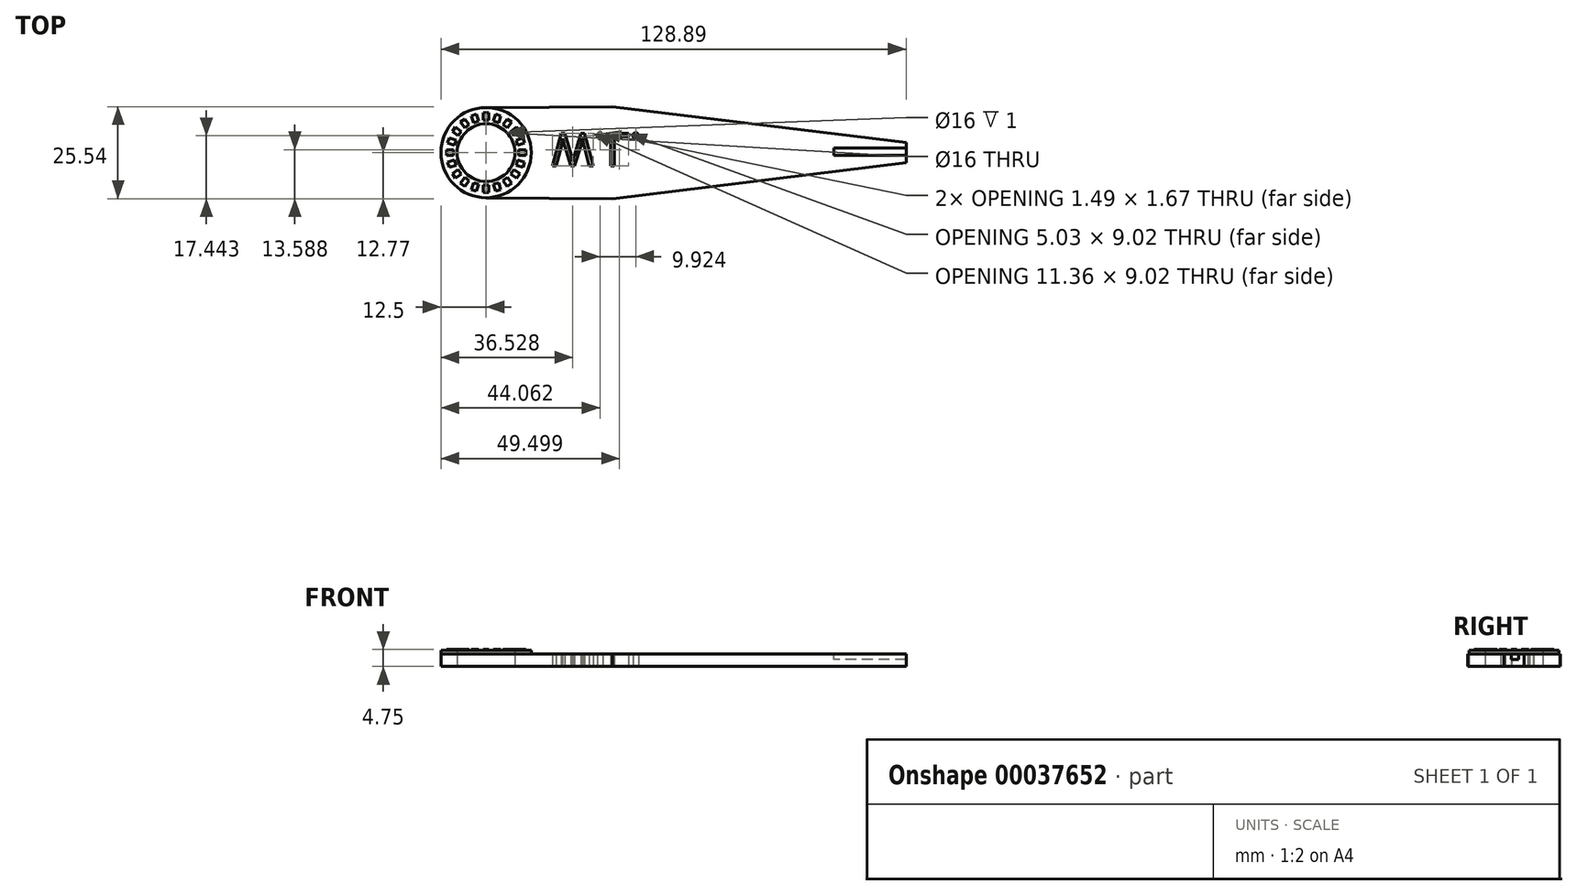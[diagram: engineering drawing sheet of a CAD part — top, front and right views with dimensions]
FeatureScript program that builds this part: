
annotation { "Feature Type Name" : "Feature", "Feature Type Description" : "" }
export const myFeature = defineFeature(function(context is Context, id is Id, definition is map)
    precondition{}
    {
        {
            var Q0;
            Q0=qCreatedBy(makeId("Top.planeOp"),FACE);
            var sketch = newSketch(context, id + "F0", { "sketchPlane" : qUnion([Q0])});
            skCircle(sketch, "E0", {"center": v(0, 0) * mm, "radius": 8 * mm});
            skCircle(sketch, "E1", {"center": v(0, 0) * mm, "radius": 12.5 * mm});
            skLineSegment(sketch, "E2", {"start": v(0, 12.5) * mm, "end": v(35, 12.77) * mm});
            skLineSegment(sketch, "E3", {"start": v(0, 0) * mm, "end": v(49.99, 0) * mm, "construction": true});
            skLineSegment(sketch, "E4.MirrorCS", {"start": v(0, -12.5) * mm, "end": v(35, -12.77) * mm});
            skLineSegment(sketch, "E5", {"start": v(35, 12.77) * mm, "end": v(117.8, 12.77) * mm, "construction": true});
            skLineSegment(sketch, "E6", {"start": v(35, 12.77) * mm, "end": v(116.39, 2.78) * mm});
            skLineSegment(sketch, "E7.MirrorCS", {"start": v(35, -12.77) * mm, "end": v(116.39, -2.78) * mm});
            skLineSegment(sketch, "E8", {"start": v(116.39, 2.78) * mm, "end": v(116.39, -2.78) * mm});
            skSolve(sketch);
        }
        {
            var Q0;
            Q0 = qSketchRegion(id + "F0", true);
            extrude(context, id + "F1", {"entities" : qUnion([Q0]), "depth" : 3.5 * mm});
        }
        {
            var Q0;
            Q0=makeQuery(id+"F1.opExtrude","CAP_FACE",FACE,{"disambiguationData":[OSD([sQuery(id+"F0.wireOp",EDGE,"E0"),sQuery(id+"F0.wireOp",EDGE,"E1"),sQuery(id+"F0.wireOp",EDGE,"E2"),sQuery(id+"F0.wireOp",EDGE,"E4.MirrorCS"),sQuery(id+"F0.wireOp",EDGE,"E6"),sQuery(id+"F0.wireOp",EDGE,"E7.MirrorCS"),sQuery(id+"F0.wireOp",EDGE,"E8")])],"isStart":false});
            var sketch = newSketch(context, id + "F2", { "sketchPlane" : qUnion([Q0])});
            skCircle(sketch, "E9", {"center": v(0, 0) * mm, "radius": 12.5 * mm});
            skCircle(sketch, "E10", {"center": v(0, 0) * mm, "radius": 8 * mm});
            skSolve(sketch);
        }
        {
            var Q0;
            Q0 = qSketchRegion(id + "F2", true);
            extrude(context, id + "F3", {"entities" : qUnion([Q0]), "depth" : 1 * mm});
        }
        {
            var Q0;
            Q0=makeQuery(id+"F3.opExtrude","CAP_FACE",FACE,{"disambiguationData":[OSD([sQuery(id+"F2.wireOp",EDGE,"E9"),sQuery(id+"F2.wireOp",EDGE,"E10")])],"isStart":false});
            var sketch = newSketch(context, id + "F4", { "sketchPlane" : qUnion([Q0])});
            skLineSegment(sketch, "E11.bottom", {"start": v(-0.75, 11) * mm, "end": v(0.75, 11) * mm});
            skLineSegment(sketch, "E11.top", {"start": v(-0.75, 9) * mm, "end": v(0.75, 9) * mm});
            skLineSegment(sketch, "E11.left", {"start": v(-0.75, 11) * mm, "end": v(-0.75, 9) * mm});
            skLineSegment(sketch, "E11.right", {"start": v(0.75, 11) * mm, "end": v(0.75, 9) * mm});
            skPoint(sketch, "E12", {"position": v(0, 8) * mm});
            skLineSegment(sketch, "E13.1.0", {"start": v(-4.11, 10.23) * mm, "end": v(-2.69, 10.7) * mm});
            skLineSegment(sketch, "E13.1.1", {"start": v(-4.11, 10.23) * mm, "end": v(-3.5, 8.33) * mm});
            skLineSegment(sketch, "E13.1.2", {"start": v(-3.5, 8.33) * mm, "end": v(-2.07, 8.8) * mm});
            skLineSegment(sketch, "E13.1.3", {"start": v(-2.69, 10.7) * mm, "end": v(-2.07, 8.8) * mm});
            skLineSegment(sketch, "E13.2.0", {"start": v(-7.07, 8.46) * mm, "end": v(-5.86, 9.34) * mm});
            skLineSegment(sketch, "E13.2.1", {"start": v(-7.07, 8.46) * mm, "end": v(-5.9, 6.84) * mm});
            skLineSegment(sketch, "E13.2.2", {"start": v(-5.9, 6.84) * mm, "end": v(-4.68, 7.72) * mm});
            skLineSegment(sketch, "E13.2.3", {"start": v(-5.86, 9.34) * mm, "end": v(-4.68, 7.72) * mm});
            skLineSegment(sketch, "E13.3.0", {"start": v(-9.34, 5.86) * mm, "end": v(-8.46, 7.07) * mm});
            skLineSegment(sketch, "E13.3.1", {"start": v(-9.34, 5.86) * mm, "end": v(-7.72, 4.68) * mm});
            skLineSegment(sketch, "E13.3.2", {"start": v(-7.72, 4.68) * mm, "end": v(-6.84, 5.9) * mm});
            skLineSegment(sketch, "E13.3.3", {"start": v(-8.46, 7.07) * mm, "end": v(-6.84, 5.9) * mm});
            skLineSegment(sketch, "E13.4.0", {"start": v(-10.7, 2.69) * mm, "end": v(-10.23, 4.11) * mm});
            skLineSegment(sketch, "E13.4.1", {"start": v(-10.7, 2.69) * mm, "end": v(-8.8, 2.07) * mm});
            skLineSegment(sketch, "E13.4.2", {"start": v(-8.8, 2.07) * mm, "end": v(-8.33, 3.5) * mm});
            skLineSegment(sketch, "E13.4.3", {"start": v(-10.23, 4.11) * mm, "end": v(-8.33, 3.5) * mm});
            skLineSegment(sketch, "E13.5.0", {"start": v(-11, -0.75) * mm, "end": v(-11, 0.75) * mm});
            skLineSegment(sketch, "E13.5.1", {"start": v(-11, -0.75) * mm, "end": v(-9, -0.75) * mm});
            skLineSegment(sketch, "E13.5.2", {"start": v(-9, -0.75) * mm, "end": v(-9, 0.75) * mm});
            skLineSegment(sketch, "E13.5.3", {"start": v(-11, 0.75) * mm, "end": v(-9, 0.75) * mm});
            skLineSegment(sketch, "E13.6.0", {"start": v(-10.23, -4.11) * mm, "end": v(-10.7, -2.69) * mm});
            skLineSegment(sketch, "E13.6.1", {"start": v(-10.23, -4.11) * mm, "end": v(-8.33, -3.5) * mm});
            skLineSegment(sketch, "E13.6.2", {"start": v(-8.33, -3.5) * mm, "end": v(-8.8, -2.07) * mm});
            skLineSegment(sketch, "E13.6.3", {"start": v(-10.7, -2.69) * mm, "end": v(-8.8, -2.07) * mm});
            skLineSegment(sketch, "E13.7.0", {"start": v(-8.46, -7.07) * mm, "end": v(-9.34, -5.86) * mm});
            skLineSegment(sketch, "E13.7.1", {"start": v(-8.46, -7.07) * mm, "end": v(-6.84, -5.9) * mm});
            skLineSegment(sketch, "E13.7.2", {"start": v(-6.84, -5.9) * mm, "end": v(-7.72, -4.68) * mm});
            skLineSegment(sketch, "E13.7.3", {"start": v(-9.34, -5.86) * mm, "end": v(-7.72, -4.68) * mm});
            skLineSegment(sketch, "E13.8.0", {"start": v(-5.86, -9.34) * mm, "end": v(-7.07, -8.46) * mm});
            skLineSegment(sketch, "E13.8.1", {"start": v(-5.86, -9.34) * mm, "end": v(-4.68, -7.72) * mm});
            skLineSegment(sketch, "E13.8.2", {"start": v(-4.68, -7.72) * mm, "end": v(-5.9, -6.84) * mm});
            skLineSegment(sketch, "E13.8.3", {"start": v(-7.07, -8.46) * mm, "end": v(-5.9, -6.84) * mm});
            skLineSegment(sketch, "E13.9.0", {"start": v(-2.69, -10.7) * mm, "end": v(-4.11, -10.23) * mm});
            skLineSegment(sketch, "E13.9.1", {"start": v(-2.69, -10.7) * mm, "end": v(-2.07, -8.8) * mm});
            skLineSegment(sketch, "E13.9.2", {"start": v(-2.07, -8.8) * mm, "end": v(-3.5, -8.33) * mm});
            skLineSegment(sketch, "E13.9.3", {"start": v(-4.11, -10.23) * mm, "end": v(-3.5, -8.33) * mm});
            skLineSegment(sketch, "E13.10.0", {"start": v(0.75, -11) * mm, "end": v(-0.75, -11) * mm});
            skLineSegment(sketch, "E13.10.1", {"start": v(0.75, -11) * mm, "end": v(0.75, -9) * mm});
            skLineSegment(sketch, "E13.10.2", {"start": v(0.75, -9) * mm, "end": v(-0.75, -9) * mm});
            skLineSegment(sketch, "E13.10.3", {"start": v(-0.75, -11) * mm, "end": v(-0.75, -9) * mm});
            skLineSegment(sketch, "E13.11.0", {"start": v(4.11, -10.23) * mm, "end": v(2.69, -10.7) * mm});
            skLineSegment(sketch, "E13.11.1", {"start": v(4.11, -10.23) * mm, "end": v(3.5, -8.33) * mm});
            skLineSegment(sketch, "E13.11.2", {"start": v(3.5, -8.33) * mm, "end": v(2.07, -8.8) * mm});
            skLineSegment(sketch, "E13.11.3", {"start": v(2.69, -10.7) * mm, "end": v(2.07, -8.8) * mm});
            skLineSegment(sketch, "E13.12.0", {"start": v(7.07, -8.46) * mm, "end": v(5.86, -9.34) * mm});
            skLineSegment(sketch, "E13.12.1", {"start": v(7.07, -8.46) * mm, "end": v(5.9, -6.84) * mm});
            skLineSegment(sketch, "E13.12.2", {"start": v(5.9, -6.84) * mm, "end": v(4.68, -7.72) * mm});
            skLineSegment(sketch, "E13.12.3", {"start": v(5.86, -9.34) * mm, "end": v(4.68, -7.72) * mm});
            skLineSegment(sketch, "E13.13.0", {"start": v(9.34, -5.86) * mm, "end": v(8.46, -7.07) * mm});
            skLineSegment(sketch, "E13.13.1", {"start": v(9.34, -5.86) * mm, "end": v(7.72, -4.68) * mm});
            skLineSegment(sketch, "E13.13.2", {"start": v(7.72, -4.68) * mm, "end": v(6.84, -5.9) * mm});
            skLineSegment(sketch, "E13.13.3", {"start": v(8.46, -7.07) * mm, "end": v(6.84, -5.9) * mm});
            skLineSegment(sketch, "E13.14.0", {"start": v(10.7, -2.69) * mm, "end": v(10.23, -4.11) * mm});
            skLineSegment(sketch, "E13.14.1", {"start": v(10.7, -2.69) * mm, "end": v(8.8, -2.07) * mm});
            skLineSegment(sketch, "E13.14.2", {"start": v(8.8, -2.07) * mm, "end": v(8.33, -3.5) * mm});
            skLineSegment(sketch, "E13.14.3", {"start": v(10.23, -4.11) * mm, "end": v(8.33, -3.5) * mm});
            skLineSegment(sketch, "E13.15.0", {"start": v(11, 0.75) * mm, "end": v(11, -0.75) * mm});
            skLineSegment(sketch, "E13.15.1", {"start": v(11, 0.75) * mm, "end": v(9, 0.75) * mm});
            skLineSegment(sketch, "E13.15.2", {"start": v(9, 0.75) * mm, "end": v(9, -0.75) * mm});
            skLineSegment(sketch, "E13.15.3", {"start": v(11, -0.75) * mm, "end": v(9, -0.75) * mm});
            skLineSegment(sketch, "E13.16.0", {"start": v(10.23, 4.11) * mm, "end": v(10.7, 2.69) * mm});
            skLineSegment(sketch, "E13.16.1", {"start": v(10.23, 4.11) * mm, "end": v(8.33, 3.5) * mm});
            skLineSegment(sketch, "E13.16.2", {"start": v(8.33, 3.5) * mm, "end": v(8.8, 2.07) * mm});
            skLineSegment(sketch, "E13.16.3", {"start": v(10.7, 2.69) * mm, "end": v(8.8, 2.07) * mm});
            skLineSegment(sketch, "E13.17.0", {"start": v(8.46, 7.07) * mm, "end": v(9.34, 5.86) * mm});
            skLineSegment(sketch, "E13.17.1", {"start": v(8.46, 7.07) * mm, "end": v(6.84, 5.9) * mm});
            skLineSegment(sketch, "E13.17.2", {"start": v(6.84, 5.9) * mm, "end": v(7.72, 4.68) * mm});
            skLineSegment(sketch, "E13.17.3", {"start": v(9.34, 5.86) * mm, "end": v(7.72, 4.68) * mm});
            skLineSegment(sketch, "E13.18.0", {"start": v(5.86, 9.34) * mm, "end": v(7.07, 8.46) * mm});
            skLineSegment(sketch, "E13.18.1", {"start": v(5.86, 9.34) * mm, "end": v(4.68, 7.72) * mm});
            skLineSegment(sketch, "E13.18.2", {"start": v(4.68, 7.72) * mm, "end": v(5.9, 6.84) * mm});
            skLineSegment(sketch, "E13.18.3", {"start": v(7.07, 8.46) * mm, "end": v(5.9, 6.84) * mm});
            skLineSegment(sketch, "E13.19.0", {"start": v(2.69, 10.7) * mm, "end": v(4.11, 10.23) * mm});
            skLineSegment(sketch, "E13.19.1", {"start": v(2.69, 10.7) * mm, "end": v(2.07, 8.8) * mm});
            skLineSegment(sketch, "E13.19.2", {"start": v(2.07, 8.8) * mm, "end": v(3.5, 8.33) * mm});
            skLineSegment(sketch, "E13.19.3", {"start": v(4.11, 10.23) * mm, "end": v(3.5, 8.33) * mm});
            skPoint(sketch, "E13.center", {"position": v(0, 0) * mm});
            skSolve(sketch);
        }
        {
            var Q0;
            Q0 = qSketchRegion(id + "F4", true);
            extrude(context, id + "F5", {"entities" : qUnion([Q0]), "operationType" : NewBodyOperationType.ADD, "depth" : .25 * mm});
        }
        {
            var Q0;
            Q0=makeQuery(id+"F1.opExtrude","CAP_FACE",FACE,{"disambiguationData":[OSD([sQuery(id+"F0.wireOp",EDGE,"E0"),sQuery(id+"F0.wireOp",EDGE,"E1"),sQuery(id+"F0.wireOp",EDGE,"E2"),sQuery(id+"F0.wireOp",EDGE,"E4.MirrorCS"),sQuery(id+"F0.wireOp",EDGE,"E6"),sQuery(id+"F0.wireOp",EDGE,"E7.MirrorCS"),sQuery(id+"F0.wireOp",EDGE,"E8")])],"isStart":false});
            var sketch = newSketch(context, id + "F6", { "sketchPlane" : qUnion([Q0])});
            skLineSegment(sketch, "E14.bottom", {"start": v(116.39, 1.28) * mm, "end": v(96.39, 1.28) * mm});
            skLineSegment(sketch, "E14.top", {"start": v(116.39, -0.72) * mm, "end": v(96.39, -0.72) * mm});
            skLineSegment(sketch, "E14.left", {"start": v(116.39, 1.28) * mm, "end": v(116.39, -0.72) * mm});
            skLineSegment(sketch, "E14.right", {"start": v(96.39, 1.28) * mm, "end": v(96.39, -0.72) * mm});
            skSolve(sketch);
        }
        {
            var Q0;
            Q0=makeQuery(id+"F1.opExtrude","CAP_FACE",FACE,{"disambiguationData":[OSD([sQuery(id+"F0.wireOp",EDGE,"E0"),sQuery(id+"F0.wireOp",EDGE,"E1"),sQuery(id+"F0.wireOp",EDGE,"E2"),sQuery(id+"F0.wireOp",EDGE,"E4.MirrorCS"),sQuery(id+"F0.wireOp",EDGE,"E6"),sQuery(id+"F0.wireOp",EDGE,"E7.MirrorCS"),sQuery(id+"F0.wireOp",EDGE,"E8")])],"isStart":true});
            var sketch = newSketch(context, id + "F7", { "sketchPlane" : qUnion([Q0])});
            skText(sketch, "E15", { "text": "W.L.", "fontName": "OpenSans-Regular.ttf"});
            const initialGuessF7  = {"E15": [0.01818, -0.00533, 1, 0, 0.0091]};
            skSetInitialGuess(sketch, initialGuessF7);
            skSolve(sketch);
        }
        {
            var Q0;
            Q0 = qSketchRegion(id + "F7", true);
            extrude(context, id + "F8", {"entities" : qUnion([Q0]), "operationType" : NewBodyOperationType.REMOVE, "endBound" : BoundingType.SYMMETRIC, "oppositeDirection" : true, "depth" : 50 * mm});
        }
        {
            var Q0;
            Q0 = qSketchRegion(id + "F6", true);
            extrude(context, id + "F9", {"entities" : qUnion([Q0]), "operationType" : NewBodyOperationType.REMOVE, "oppositeDirection" : true, "depth" : 1.5 * mm});
        }
    });
